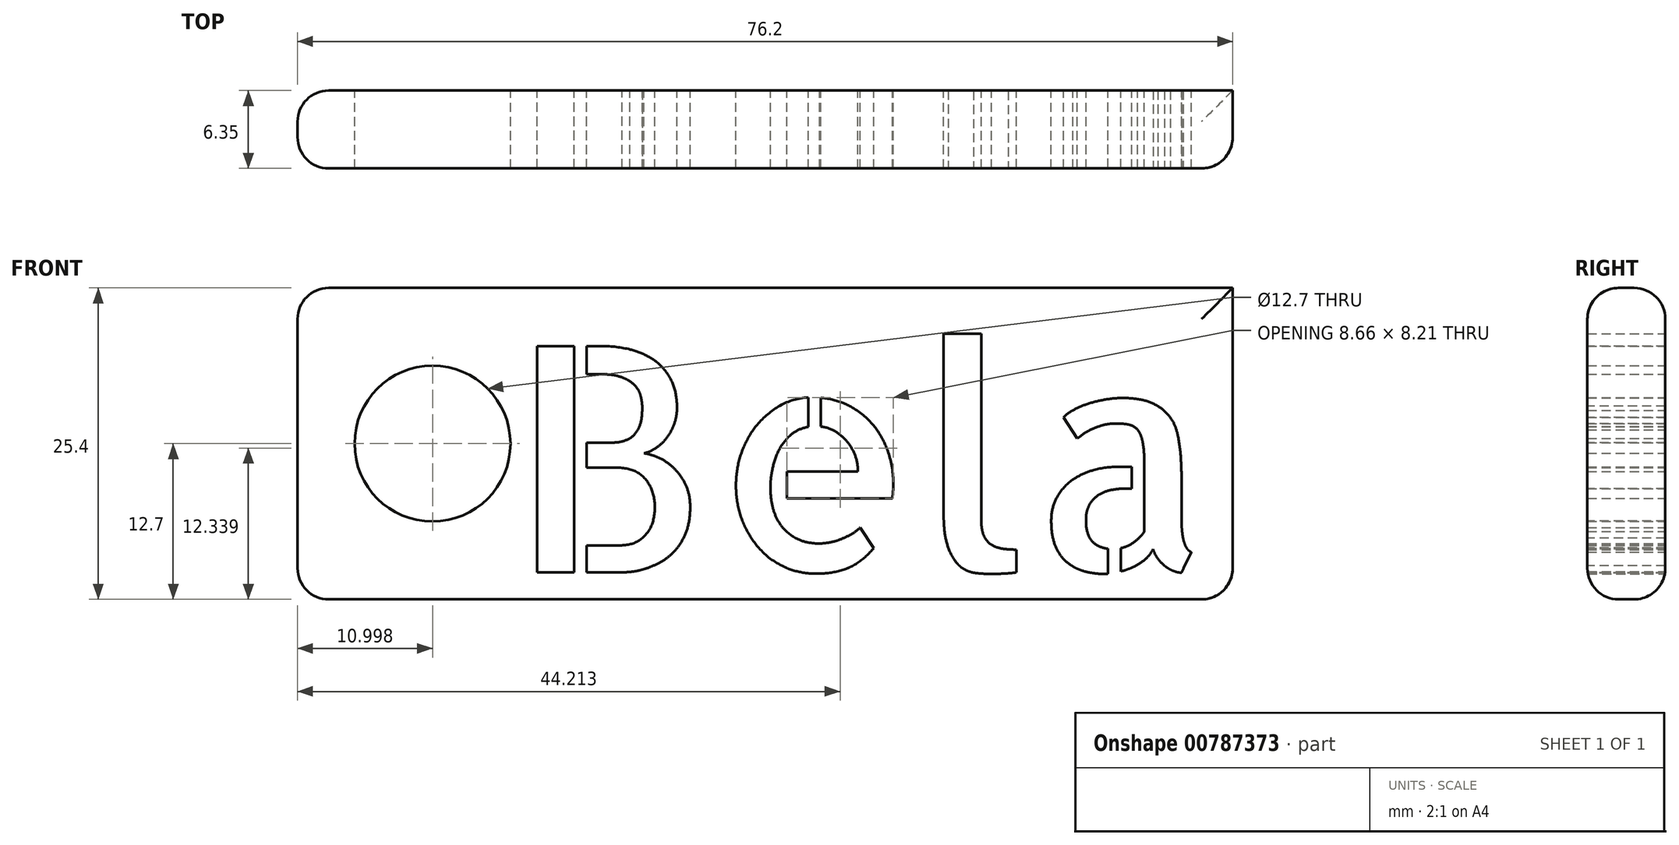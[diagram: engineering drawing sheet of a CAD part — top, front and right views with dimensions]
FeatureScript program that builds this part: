
annotation { "Feature Type Name" : "Feature", "Feature Type Description" : "" }
export const myFeature = defineFeature(function(context is Context, id is Id, definition is map)
    precondition{}
    {
        {
            var Q0;
            Q0=qCreatedBy(makeId("Front.planeOp"),FACE);
            var sketch = newSketch(context, id + "F0", { "sketchPlane" : qUnion([Q0])});
            skLineSegment(sketch, "E0.bottom", {"start": v(38.1, 12.7) * mm, "end": v(-38.1, 12.7) * mm});
            skLineSegment(sketch, "E0.top", {"start": v(38.1, -12.7) * mm, "end": v(-38.1, -12.7) * mm});
            skLineSegment(sketch, "E0.left", {"start": v(38.1, 12.7) * mm, "end": v(38.1, -12.7) * mm});
            skLineSegment(sketch, "E0.right", {"start": v(-38.1, 12.7) * mm, "end": v(-38.1, -12.7) * mm});
            skPoint(sketch, "E0.middle", {"position": v(0, 0) * mm});
            skCircle(sketch, "E1", {"center": v(-27.1, 0) * mm, "radius": 6.35 * mm});
            skText(sketch, "E2", { "text": "Bela", "fontName": "AllertaStencil-Regular.ttf"});
            const initialGuessF0  = {"E2": [-0.02098, -0.0105, 1, 0, 0.01846]};
            skSetInitialGuess(sketch, initialGuessF0);
            skSolve(sketch);
        }
        {
            var Q0;
            Q0=makeQuery(id+"F0.imprint","IMPRINT",FACE,{"disambiguationData":[TD([[makeQuery(id+"F0.imprint","IMPRINT",EDGE,{"derivedFrom":sQuery(id+"F0.wireOp",EDGE,"E0.bottom")}),1.0]])]});
            extrude(context, id + "F1", {"entities" : qUnion([Q0]), "depth" : 6.35 * mm, "offsetDistance" : 25.4 * mm});
        }
        {
            var Q0;
            Q0=makeQuery(id+"F1.opExtrude","CAP_EDGE",EDGE,{"disambiguationData":[OSD([sQuery(id+"F0.wireOp",EDGE,"E0.left")])],"isStart":false});
            var Q1;
            Q1=makeQuery(id+"F1.opExtrude","SWEPT_EDGE",EDGE,{"disambiguationData":[OSD([sQuery(id+"F0.wireOp",EDGE,"E0.top"),sQuery(id+"F0.wireOp",EDGE,"E0.left")])]});
            var Q2;
            Q2=makeQuery(id+"F1.opExtrude","CAP_EDGE",EDGE,{"disambiguationData":[OSD([sQuery(id+"F0.wireOp",EDGE,"E0.top")])],"isStart":true});
            var Q3;
            Q3=makeQuery(id+"F1.opExtrude","CAP_EDGE",EDGE,{"disambiguationData":[OSD([sQuery(id+"F0.wireOp",EDGE,"E0.top")])],"isStart":false});
            var Q4;
            Q4=makeQuery(id+"F1.opExtrude","SWEPT_EDGE",EDGE,{"disambiguationData":[OSD([sQuery(id+"F0.wireOp",EDGE,"E0.top"),sQuery(id+"F0.wireOp",EDGE,"E0.right")])]});
            var Q5;
            Q5=makeQuery(id+"F1.opExtrude","CAP_EDGE",EDGE,{"disambiguationData":[OSD([sQuery(id+"F0.wireOp",EDGE,"E0.right")])],"isStart":false});
            var Q6;
            Q6=makeQuery(id+"F1.opExtrude","SWEPT_EDGE",EDGE,{"disambiguationData":[OSD([sQuery(id+"F0.wireOp",EDGE,"E0.bottom"),sQuery(id+"F0.wireOp",EDGE,"E0.right")])]});
            var Q7;
            Q7=makeQuery(id+"F1.opExtrude","CAP_EDGE",EDGE,{"disambiguationData":[OSD([sQuery(id+"F0.wireOp",EDGE,"E0.right")])],"isStart":true});
            var Q8;
            Q8=makeQuery(id+"F1.opExtrude","CAP_EDGE",EDGE,{"disambiguationData":[OSD([sQuery(id+"F0.wireOp",EDGE,"E0.bottom")])],"isStart":false});
            var Q9;
            Q9=makeQuery(id+"F1.opExtrude","CAP_EDGE",EDGE,{"disambiguationData":[OSD([sQuery(id+"F0.wireOp",EDGE,"E0.bottom")])],"isStart":true});
            fillet(context, id + "F2", {"entities" : qUnion([Q0, Q1, Q2, Q3, Q4, Q5, Q6, Q7, Q8, Q9]), "radius" : 2.54 * mm, "tangentPropagation" : true, "allowEdgeOverflow" : false});
        }
    });
